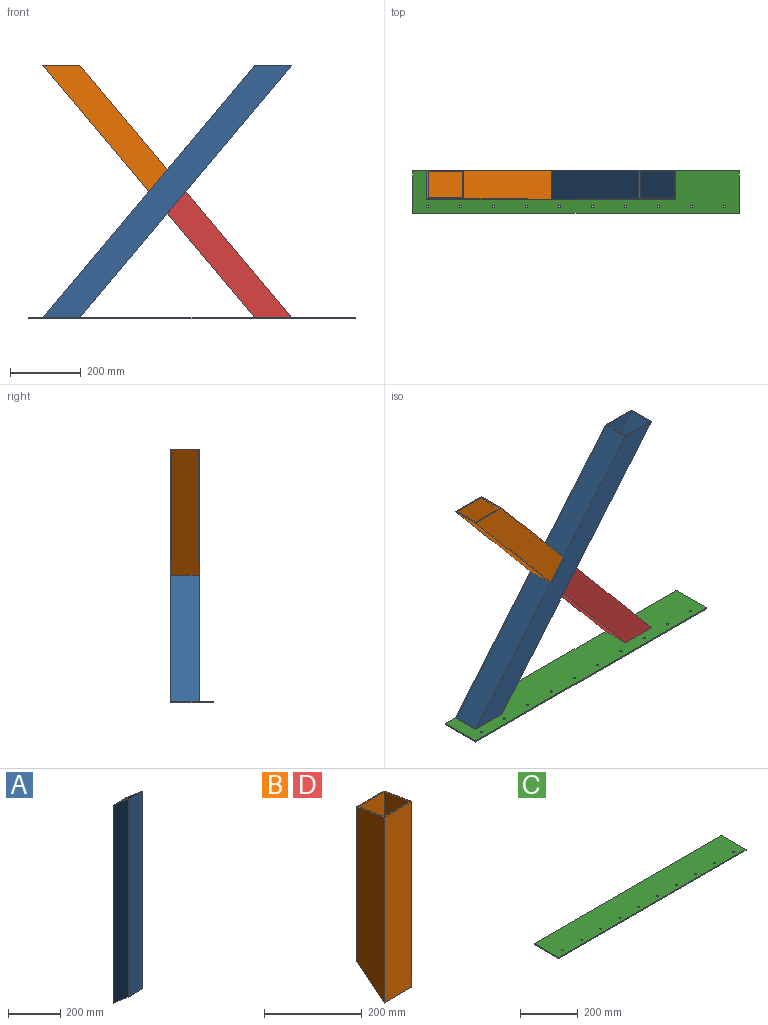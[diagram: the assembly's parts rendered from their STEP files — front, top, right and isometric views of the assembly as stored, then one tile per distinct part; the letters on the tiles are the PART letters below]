
ASSEMBLY  parts=4 mates=8
PART A: 10 faces, bbox 80x80x997.3 mm
  f0: plane 992.29x74mm, normal (-1,0,0), area 68834.2mm2, adj f1,f3,f4,f5
  f1: plane 930.19x74mm, normal (0,-1,0), area 68834.2mm2, adj f0,f2,f4,f5
  f2: plane 992.29x74mm, normal (1,0,0), area 68834.2mm2, adj f1,f3,f4,f5
  f3: plane 930.19x74mm, normal (0,1,0), area 68834.2mm2, adj f0,f2,f4,f5
  f4: plane 80x80mm, normal (0,0.64,0.77), area 1206.2mm2, adj f0,f1,f2,f3,f6,f7,f8,f9
  f5: plane 80x80mm, normal (0,-0.64,-0.77), area 1206.2mm2, adj f0,f1,f2,f3,f6,f7,f8,f9
  f6: plane 997.32x80mm, normal (-1,0,0), area 74415.4mm2, adj f4,f5,f7,f9
  f7: plane 930.19x80mm, normal (0,-1,0), area 74415.4mm2, adj f4,f5,f6,f8
  f8: plane 997.32x80mm, normal (1,0,0), area 74415.4mm2, adj f4,f5,f7,f9
  f9: plane 930.19x80mm, normal (0,1,0), area 74415.4mm2, adj f4,f5,f6,f8
PART B: 10 faces, bbox 80x80x465 mm
  f0: plane 461.95x74mm, normal (-1,0,0), area 31404.3mm2, adj f1,f3,f4,f5
  f1: plane 386.81x74mm, normal (0,-1,0), area 28624.1mm2, adj f0,f2,f4,f5
  f2: plane 461.95x74mm, normal (1,0,0), area 31404.3mm2, adj f1,f3,f4,f5
  f3: plane 461.95x74mm, normal (0,1,0), area 34184.6mm2, adj f0,f2,f4,f5
  f4: plane 80x80mm, normal (0,0.17,0.98), area 938.3mm2, adj f0,f1,f2,f3,f6,f7,f8,f9
  f5: plane 80x80mm, normal (0,0.64,-0.77), area 1206.2mm2, adj f0,f1,f2,f3,f6,f7,f8,f9
  f6: plane 383.77x80mm, normal (0,1,0), area 30701.3mm2, adj f4,f5,f7,f9
  f7: plane 465x80mm, normal (-1,0,0), area 33950.6mm2, adj f4,f5,f6,f8
  f8: plane 465x80mm, normal (0,-1,0), area 37200mm2, adj f4,f5,f7,f9
  f9: plane 465x80mm, normal (1,0,0), area 33950.6mm2, adj f4,f5,f6,f8
PART C: 16 faces, bbox 920x120x4 mm
  f0: plane 120x4mm, normal (-1,0,0), area 480mm2, adj f1,f12,f14,f15
  f1: plane 920x4mm, normal (0,-1,0), area 3680mm2, adj f0,f2,f14,f15
  f2: plane 120x4mm, normal (1,0,0), area 480mm2, adj f1,f12,f14,f15
  f3: cylinder r=3mm len=6mm, axis (0,0,-1), area 75.4mm2, adj f14,f15
  f4: cylinder r=3mm len=6mm, axis (0,0,-1), area 75.4mm2, adj f14,f15
  f5: cylinder r=3mm len=6mm, axis (0,0,-1), area 75.4mm2, adj f14,f15
  f6: cylinder r=3mm len=6mm, axis (0,0,-1), area 75.4mm2, adj f14,f15
  f7: cylinder r=3mm len=6mm, axis (0,0,-1), area 75.4mm2, adj f14,f15
  f8: cylinder r=3mm len=6mm, axis (0,0,-1), area 75.4mm2, adj f14,f15
  f9: cylinder r=3mm len=6mm, axis (0,0,-1), area 75.4mm2, adj f14,f15
  f10: cylinder r=3mm len=6mm, axis (0,0,-1), area 75.4mm2, adj f14,f15
  f11: cylinder r=3mm len=6mm, axis (0,0,-1), area 75.4mm2, adj f14,f15
  f12: plane 920x4mm, normal (0,1,0), area 3680mm2, adj f0,f2,f14,f15
  f13: cylinder r=3mm len=6mm, axis (0,0,-1), area 75.4mm2, adj f14,f15
  f14: plane 920x120mm, normal (0,0,1), area 110117.3mm2, adj f0,f1,f2,f3,f4,f5,f6,f7
  f15: plane 920x120mm, normal (0,0,-1), area 110117.3mm2, adj f0,f1,f2,f3,f4,f5,f6,f7
PART D: same geometry as B
PLACE A rot(axis=(0.32,0.32,0.89),96.7deg) t=(-205.12,251.91,611.32)mm
PLACE B rot(axis=(0.68,0.68,0.25),152deg) t=(-266.28,251.91,1375.31)mm
PLACE C t=(-305.59,211.91,658.74)mm fixed
PLACE D rot(axis=(-0.32,-0.32,0.89),96.7deg) t=(435.82,251.91,662.74)mm
MATE planar A.f6 <-> B.f7  axis (0,-1,0) through (136.98,251.91,1019.03)mm
MATE planar A.f9 <-> B.f4  axis (-0.77,0,0.64) through (32.55,291.91,1019.03)mm
MATE planar A.f5 <-> C.f14  axis (0,0,-1) through (-214.19,291.91,662.74)mm
MATE planar B.f5 <-> A.f4  axis (0,0,1) through (-214.07,291.91,1375.31)mm
MATE planar A.f8 <-> C.f12  axis (0,1,0) through (84.77,331.91,1019.03)mm
MATE planar D.f4 <-> A.f7  axis (-0.77,0,0.64) through (110.81,291.91,987.84)mm
MATE planar D.f5 <-> A.f5  axis (0,0,-1) through (335.3,254.91,662.74)mm
MATE planar D.f7 <-> A.f6  axis (0,-1,0) through (248.46,251.91,825.79)mm
